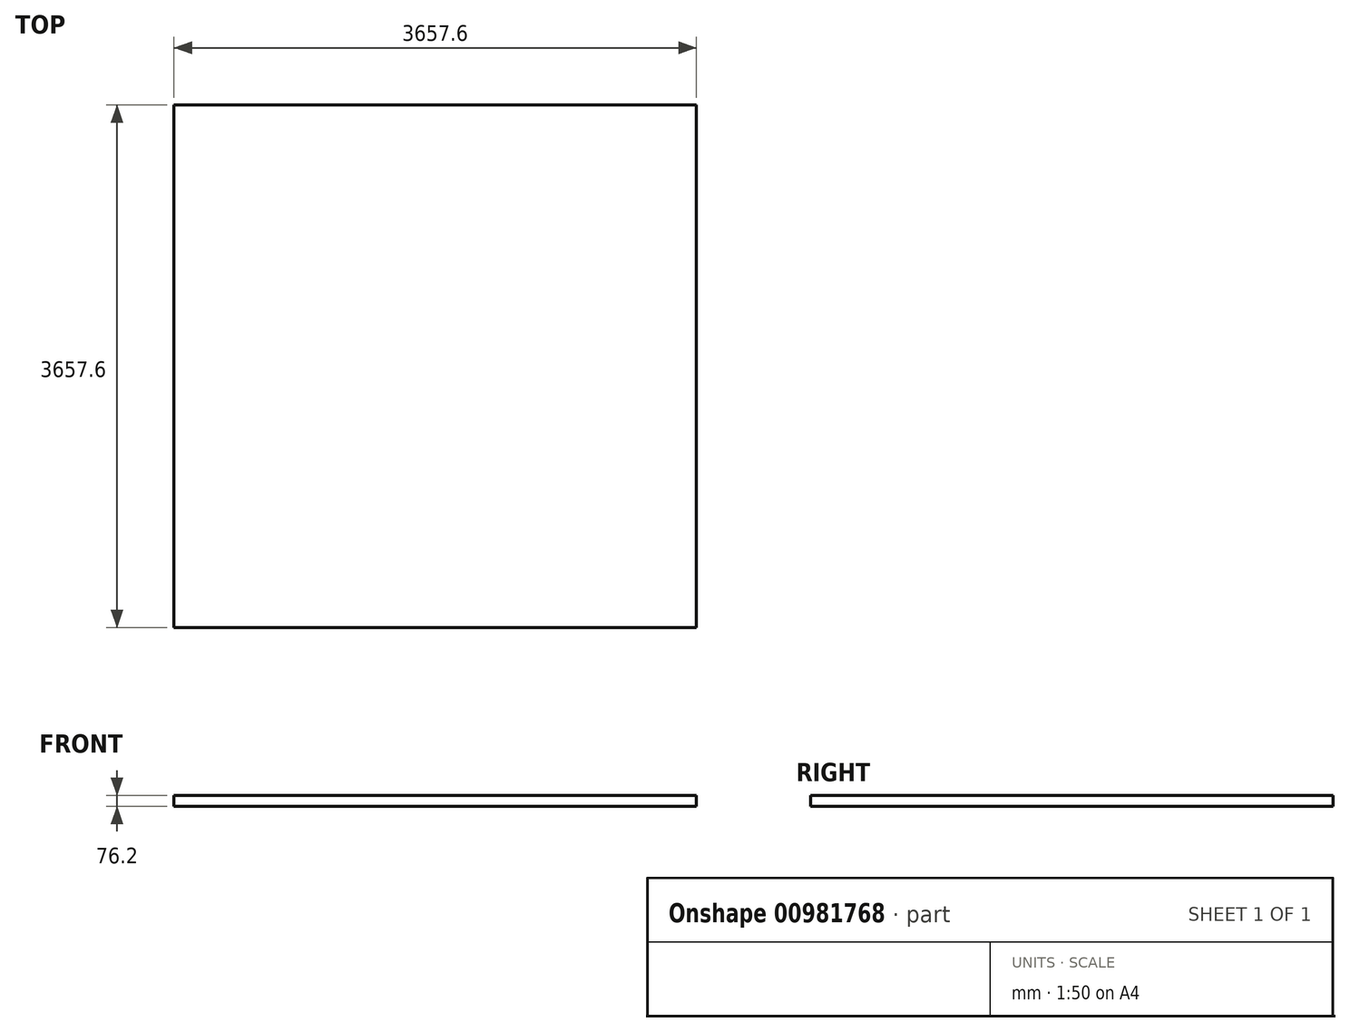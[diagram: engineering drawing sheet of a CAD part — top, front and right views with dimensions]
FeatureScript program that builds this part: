
annotation { "Feature Type Name" : "Feature", "Feature Type Description" : "" }
export const myFeature = defineFeature(function(context is Context, id is Id, definition is map)
    precondition{}
    {
        {
            var Q0;
            Q0=qCreatedBy(makeId("Top.planeOp"),FACE);
            var sketch = newSketch(context, id + "F0", { "sketchPlane" : qUnion([Q0])});
            skLineSegment(sketch, "E0.bottom", {"start": v(1828.8, -1828.8) * mm, "end": v(-1828.8, -1828.8) * mm});
            skLineSegment(sketch, "E0.top", {"start": v(1828.8, 1828.8) * mm, "end": v(-1828.8, 1828.8) * mm});
            skLineSegment(sketch, "E0.left", {"start": v(1828.8, -1828.8) * mm, "end": v(1828.8, 1828.8) * mm});
            skLineSegment(sketch, "E0.right", {"start": v(-1828.8, -1828.8) * mm, "end": v(-1828.8, 1828.8) * mm});
            skPoint(sketch, "E0.middle", {"position": v(0, 0) * mm});
            skSolve(sketch);
        }
        {
            var Q0;
            Q0 = qSketchRegion(id + "F0", true);
            extrude(context, id + "F1", {"entities" : qUnion([Q0]), "depth" : 76.2 * mm, "offsetDistance" : 25.4 * mm});
        }
    });
